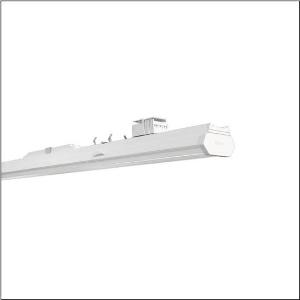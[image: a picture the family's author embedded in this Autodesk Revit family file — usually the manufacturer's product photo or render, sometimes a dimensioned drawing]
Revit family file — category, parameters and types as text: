
# Revit family: licross_11_protected_mo_51td1bdn69xg
name_source: partatom
category: Lighting Fixtures
units: mm (PartAtom-declared; Revit-internal decimal feet)

## family parameters
Cut with Voids When Loaded = No
Host = Face
Light Source = No
Part Type = Normal
Room Calculation Point = No
Round Connector Dimension = Use Diameter
Shared = No

## types (1)
- --- (1 x LED, 9140 lm, 57.1 W, 6500K)
    Apparent Load = 57 VA
    CIE Flux Codes = 54 82 95 97 100
    Color Rendering = 80
    Color Temperature = 6500K
    Default Elevation = 1800 mm
    Description = Licross 11 Protected MO, luminaire insert, of sheet steel, galvanised, coil coated, white, length: 1.500mm, width: 90mm, height: 101mm, LED rated luminous flux: 9.140lm, light colour: 865, SDCM (Standard Deviation of Colour Matching)MacAdam ≤ 2 SDCM (initial), control gear: DALI 2, with plug, 5-pole, with phase selection, mains connection: 220..240V, AC, 50/60Hz, rated input power: 57W, internal wiring halogen-free, primary optical cover: cover, of PMMA, light emission: direct distribution, primary light characteristic: symmetric, protection rating (complete): IP54, insulation class (complete): insulation class I (protective earthing), certification: CE, ENEC, VDE, UKCA, protection symbol: D if used in an environment with non-conductive dust loads with corresponding accessories, impact resistance: IK06, permissible ambient temperature for indoor applications: -25..+35°C, corresponds to IFS (International Featured Standards) requirements for safety and quality in the food industry, reducing of maximum allowable ambient temperature of 5°C with ceiling mounting, LABS conformity tested according to VDMA 24364:2018-05, The light source and the operating device comply with the requirements of the Ecodesign Regulation (EU) 2019/2020 and are replaceable in accordance with this regulation, packaging unit: 1 piece
    Height = 92 mm
    Lamp = 1 x LED
    Lamp Light Flux = 9140 lm
    Lamp Power = 57.1 W
    Lamp count = 1
    Length = 1500 mm
    Luminous efficacy = 160 lm/W
    Manufacturer = Siteco
    ModVariant = No
    Model = 51TD1BDN69XG
    Mounting Place = Ceiling
    Mounting Type = Pendant
    Number of Poles = 1
    OnlyDefault = Yes
    Power Factor = 1
    Product Name = Licross 11 Protected MO
    Product group = luminaire insert | ceiling pendant
    ProductGroupID = 901
    Protection Class = Protection class I
    Protection Degree = IP 54
    RLX_Detail_Level = 1
    RLX_Emergency_Light_Flux = 0 lm
    RLX_Emergency_Type = 0
    RLX_Emergency_Type_DB = No
    RlxData = <blob elided: 24549 chars, md5=bd62557e>
    Socket = socket
    Standby Power = 0 W
    System Light Flux = 9140 lm
    System Power = 57 W
    Type Comments = factory setting: luminous flux: 100 % | dim-lin: 254 | 378 mA
    Type Image = l_1256145.jpg
    URL = http://relux.com
    VarID = @adj_077259
    Voltage = 0 V
    Weight = 0.00 kg
    Width = 88 mm

## geometry (parser evidence)
native form markers: Blend x4, Sweep x10
no freeform markers — native parametric forms only
